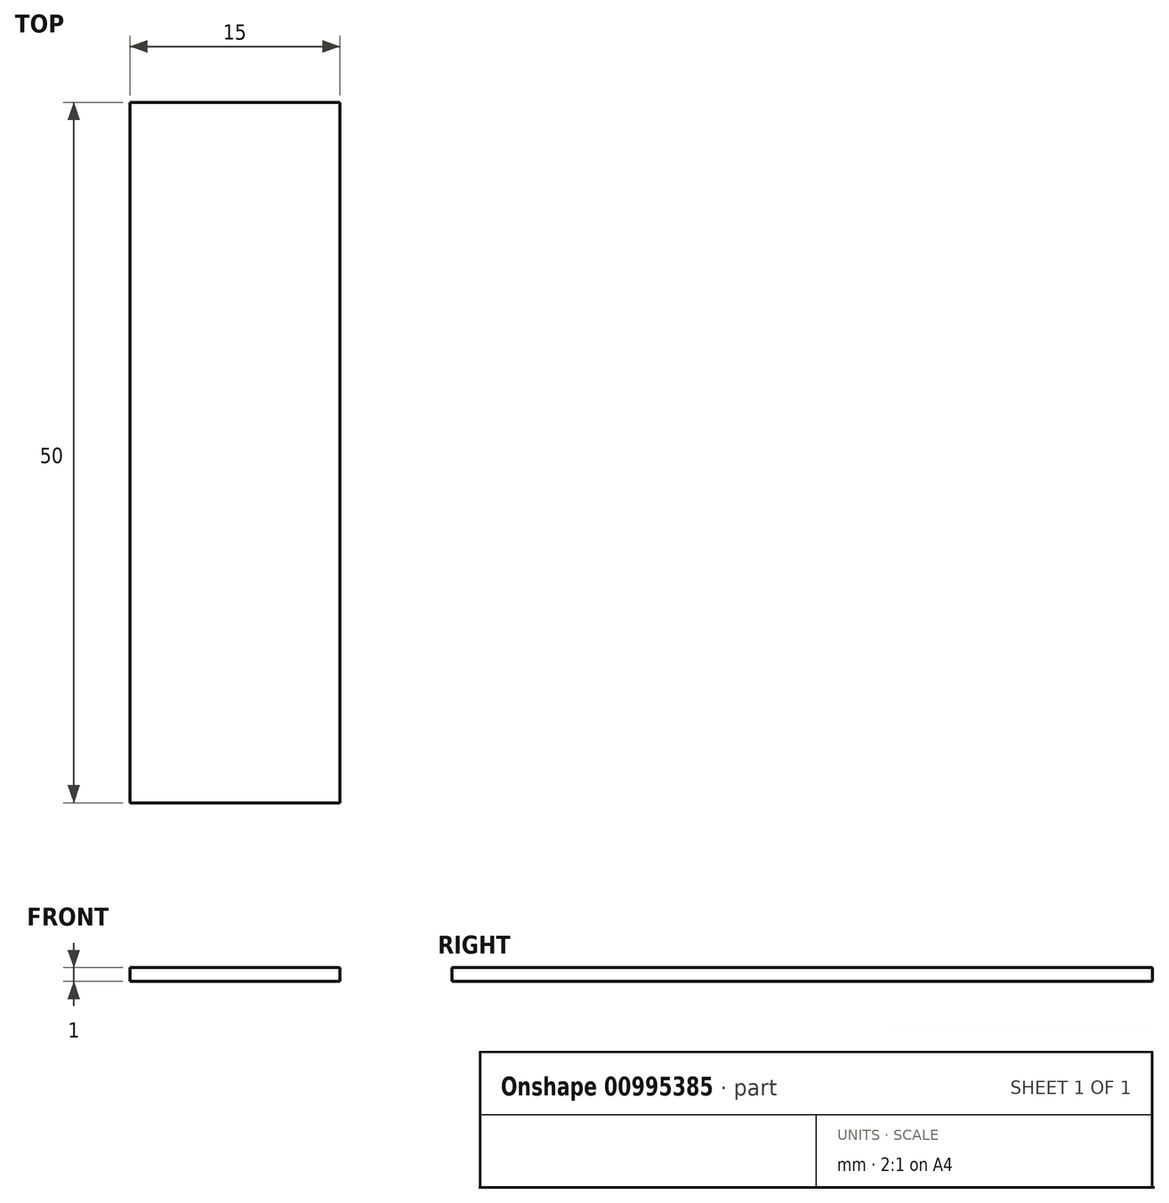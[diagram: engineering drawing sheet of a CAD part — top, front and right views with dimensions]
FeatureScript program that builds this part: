
annotation { "Feature Type Name" : "Feature", "Feature Type Description" : "" }
export const myFeature = defineFeature(function(context is Context, id is Id, definition is map)
    precondition{}
    {
        {
            var Q0;
            Q0=qCreatedBy(makeId("Top.planeOp"),FACE);
            var sketch = newSketch(context, id + "F0", { "sketchPlane" : qUnion([Q0])});
            skLineSegment(sketch, "E0.bottom", {"start": v(-7.5, -25) * mm, "end": v(7.5, -25) * mm});
            skLineSegment(sketch, "E0.top", {"start": v(-7.5, 25) * mm, "end": v(7.5, 25) * mm});
            skLineSegment(sketch, "E0.left", {"start": v(-7.5, -25) * mm, "end": v(-7.5, 25) * mm});
            skLineSegment(sketch, "E0.right", {"start": v(7.5, -25) * mm, "end": v(7.5, 25) * mm});
            skPoint(sketch, "E0.middle", {"position": v(0, 0) * mm});
            skSolve(sketch);
        }
        {
            var Q0;
            Q0=makeQuery(id+"F0.imprint","IMPRINT",FACE,{"disambiguationData":[TD([[makeQuery(id+"F0.imprint","IMPRINT",EDGE,{"derivedFrom":sQuery(id+"F0.wireOp",EDGE,"E0.bottom")}),1.0]])]});
            extrude(context, id + "F1", {"entities" : qUnion([Q0]), "depth" : 1 * mm, "offsetDistance" : 25 * mm});
        }
    });
